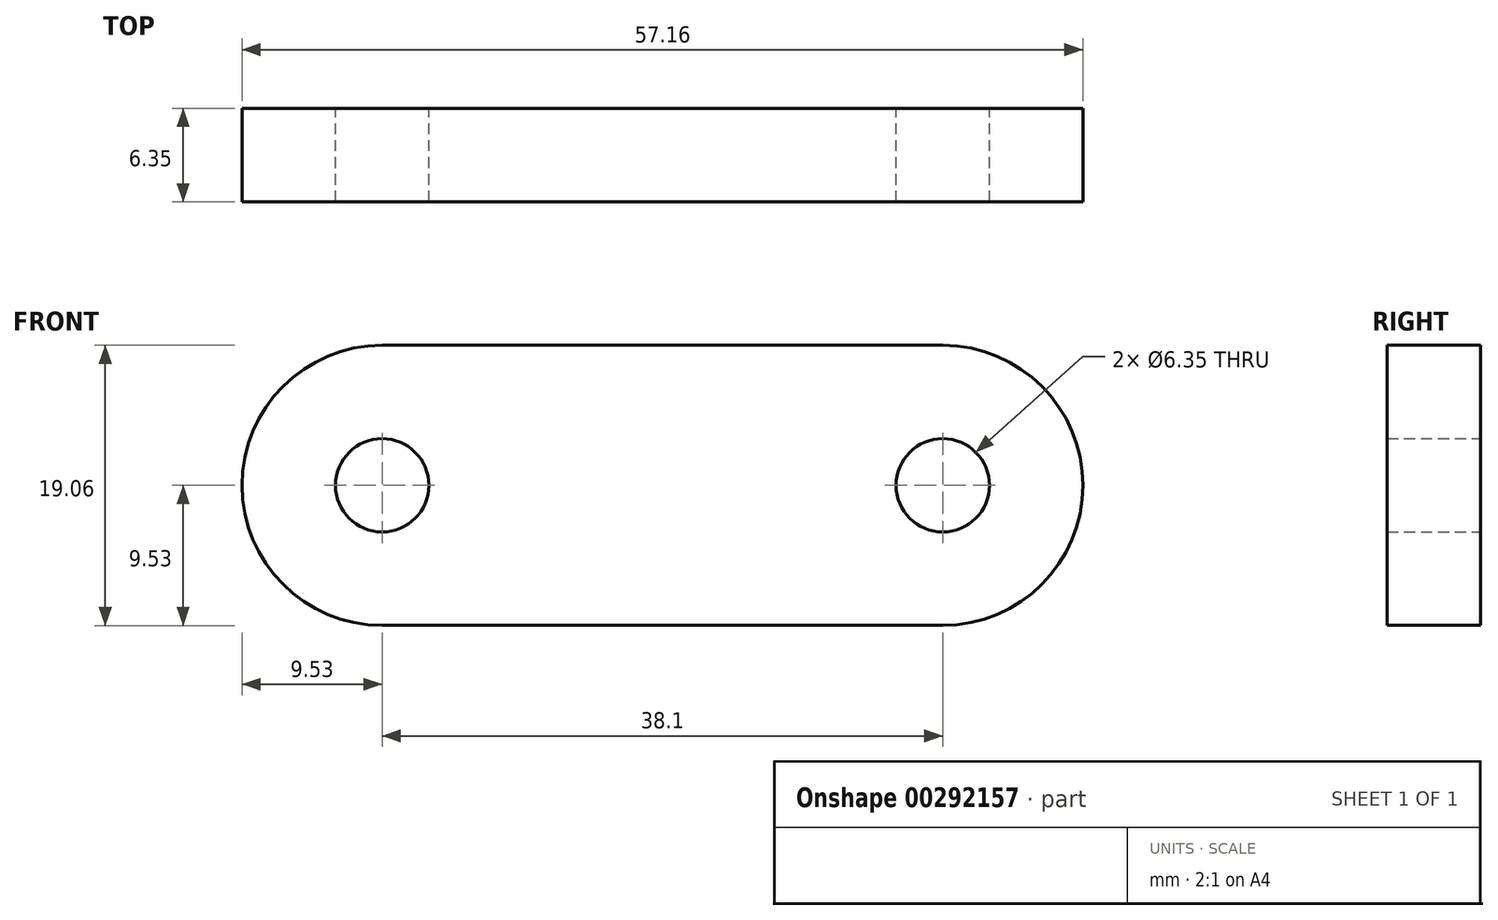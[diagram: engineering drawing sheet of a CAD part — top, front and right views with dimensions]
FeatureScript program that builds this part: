
annotation { "Feature Type Name" : "Feature", "Feature Type Description" : "" }
export const myFeature = defineFeature(function(context is Context, id is Id, definition is map)
    precondition{}
    {
        {
            var Q0;
            Q0=qCreatedBy(makeId("Front.planeOp"),FACE);
            var sketch = newSketch(context, id + "F0", { "sketchPlane" : qUnion([Q0])});
            skLineSegment(sketch, "E0.bottom", {"start": v(19.05, -9.53) * mm, "end": v(-19.05, -9.53) * mm});
            skLineSegment(sketch, "E0.top", {"start": v(19.05, 9.52) * mm, "end": v(-19.05, 9.52) * mm});
            skPoint(sketch, "E0.middle", {"position": v(0, 0) * mm});
            skArc(sketch, "E1", {"start": v(19.05, -9.53) * mm, "mid": v(28.58, 0) * mm, "end": v(19.05, 9.52) * mm});
            skArc(sketch, "E2", {"start": v(-19.05, 9.52) * mm, "mid": v(-28.57, 0) * mm, "end": v(-19.05, -9.53) * mm});
            skCircle(sketch, "E3", {"center": v(-19.05, 0) * mm, "radius": 3.18 * mm});
            skCircle(sketch, "E4", {"center": v(19.05, 0) * mm, "radius": 3.18 * mm});
            skSolve(sketch);
        }
        {
            var Q0;
            Q0=makeQuery(id+"F0.imprint","IMPRINT",FACE,{"disambiguationData":[TD([[makeQuery(id+"F0.imprint","IMPRINT",EDGE,{"derivedFrom":sQuery(id+"F0.wireOp",EDGE,"E0.bottom")}),-1.0]])]});
            extrude(context, id + "F1", {"entities" : qUnion([Q0]), "depth" : 6.35 * mm});
        }
    });
